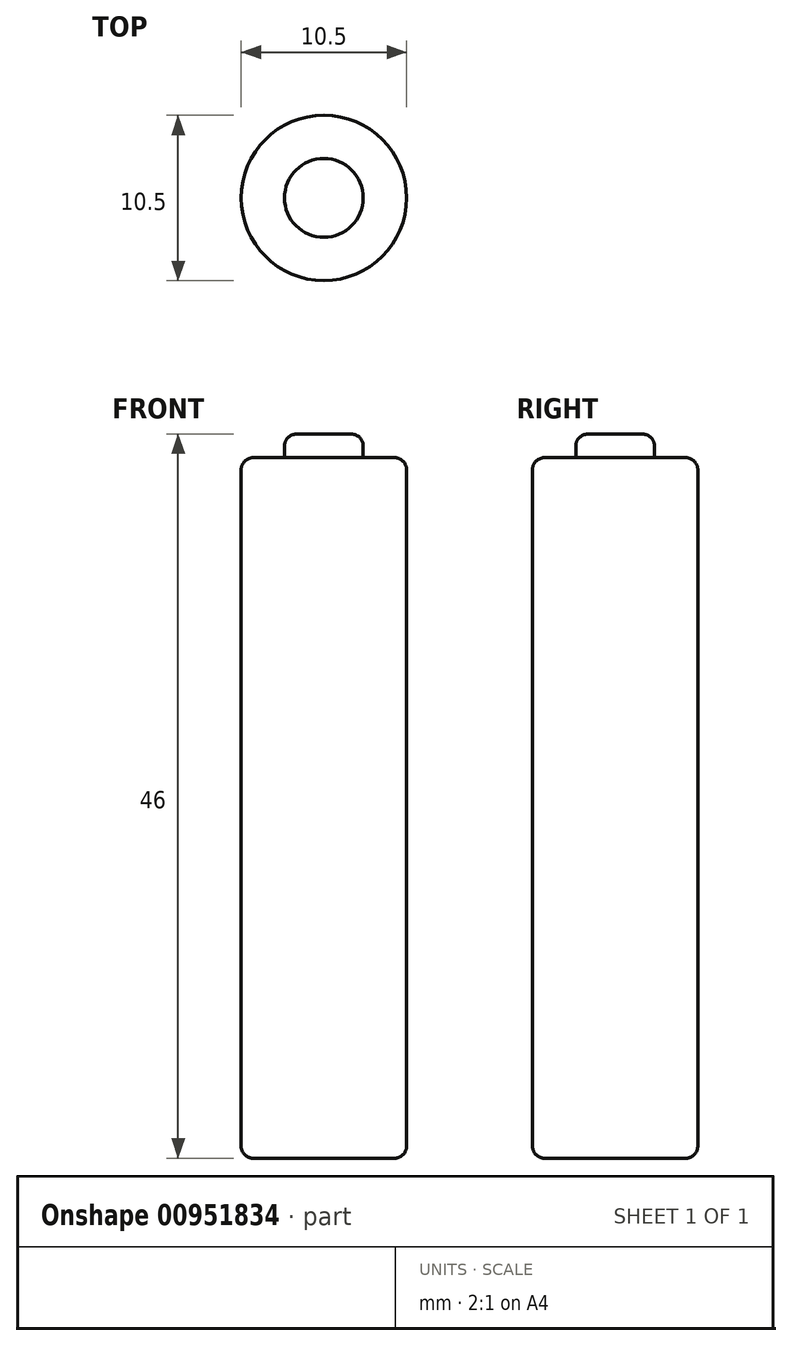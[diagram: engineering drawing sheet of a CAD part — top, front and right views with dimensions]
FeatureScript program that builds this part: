
annotation { "Feature Type Name" : "Feature", "Feature Type Description" : "" }
export const myFeature = defineFeature(function(context is Context, id is Id, definition is map)
    precondition{}
    {
        {
            var Q0;
            Q0=qCreatedBy(makeId("Top.planeOp"),FACE);
            var sketch = newSketch(context, id + "F0", { "sketchPlane" : qUnion([Q0])});
            skCircle(sketch, "E0", {"center": v(0, 0) * mm, "radius": 5.25 * mm});
            skSolve(sketch);
        }
        {
            var Q0;
            Q0=makeQuery(id+"F0.imprint","IMPRINT",FACE,{"disambiguationData":[TD([[makeQuery(id+"F0.imprint","IMPRINT",EDGE,{"derivedFrom":sQuery(id+"F0.wireOp",EDGE,"E0")}),1.0]])]});
            extrude(context, id + "F1", {"entities" : qUnion([Q0]), "endBound" : BoundingType.SYMMETRIC, "depth" : 44.5 * mm, "offsetDistance" : 25.4 * mm});
        }
        {
            var Q0;
            Q0=makeQuery(id+"F1.opExtrude","CAP_FACE",FACE,{"disambiguationData":[OSD([sQuery(id+"F0.wireOp",EDGE,"E0")])],"isStart":false});
            var sketch = newSketch(context, id + "F2", { "sketchPlane" : qUnion([Q0])});
            skCircle(sketch, "E1", {"center": v(0, 0) * mm, "radius": 2.5 * mm});
            skSolve(sketch);
        }
        {
            var Q0;
            Q0 = qSketchRegion(id + "F2", true);
            extrude(context, id + "F3", {"entities" : qUnion([Q0]), "operationType" : NewBodyOperationType.ADD, "depth" : 1.5 * mm, "offsetDistance" : 25.4 * mm});
        }
        {
            var Q0;
            Q0=makeQuery(id+"F3.opExtrude","CAP_EDGE",EDGE,{"disambiguationData":[OSD([sQuery(id+"F2.wireOp",EDGE,"E1")])],"isStart":false});
            var Q1;
            Q1=makeQuery(id+"F1.opExtrude","CAP_EDGE",EDGE,{"disambiguationData":[OSD([sQuery(id+"F0.wireOp",EDGE,"E0")])],"isStart":true});
            var Q2;
            Q2=makeQuery(id+"F1.opExtrude","CAP_EDGE",EDGE,{"disambiguationData":[OSD([sQuery(id+"F0.wireOp",EDGE,"E0")])],"isStart":false});
            fillet(context, id + "F4", {"entities" : qUnion([Q0, Q1, Q2]), "radius" : 0.76 * mm, "tangentPropagation" : true, "allowEdgeOverflow" : false});
        }
    });
